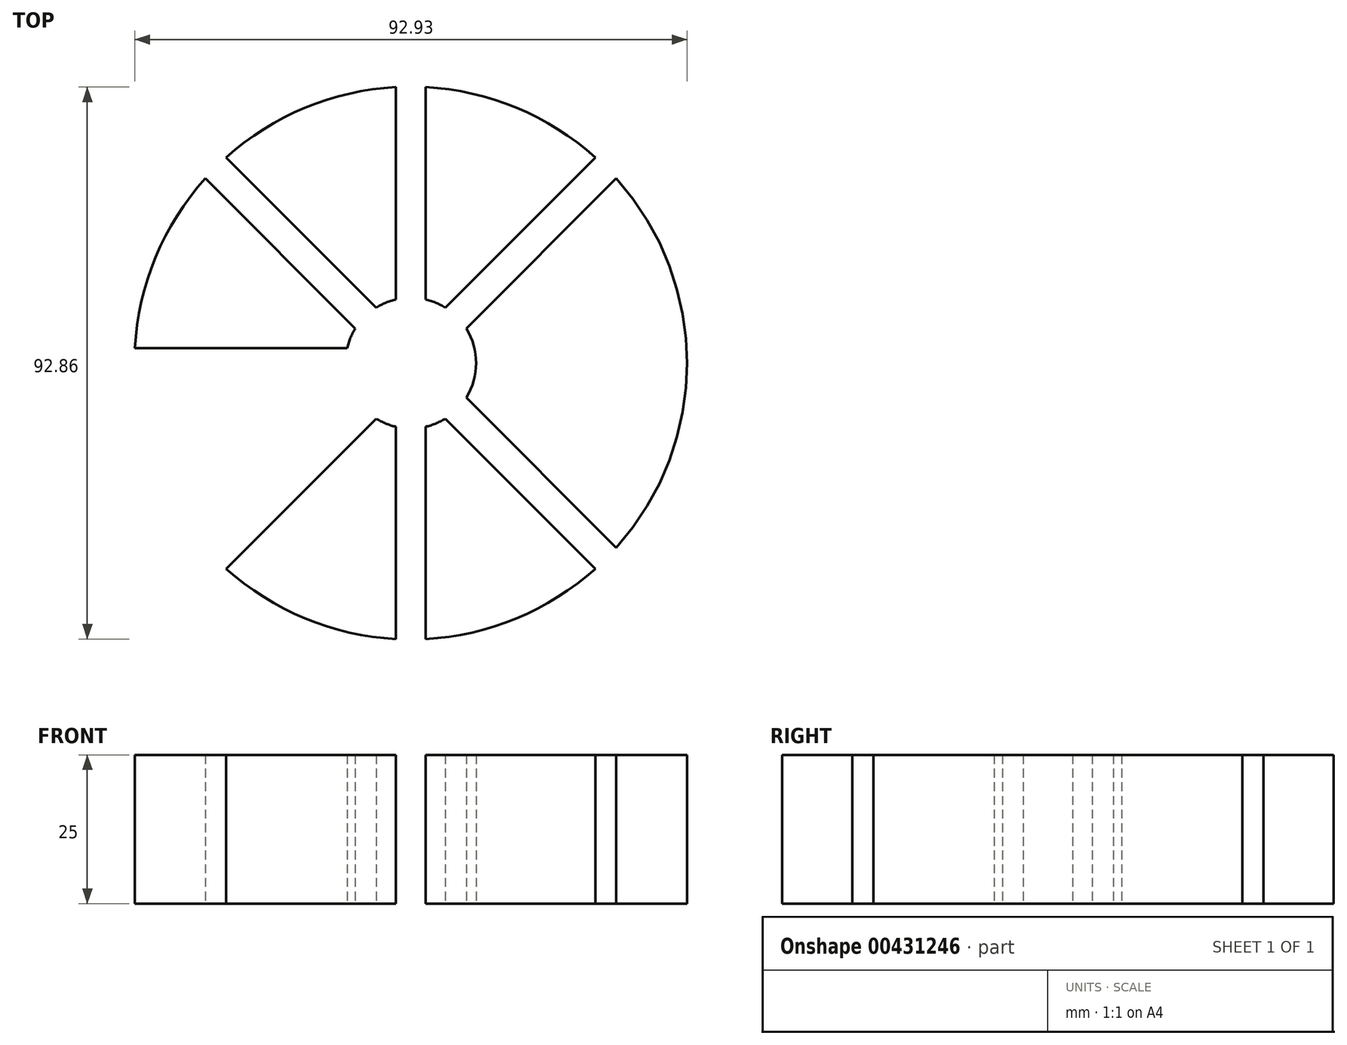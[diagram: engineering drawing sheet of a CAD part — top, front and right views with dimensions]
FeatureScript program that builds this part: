
annotation { "Feature Type Name" : "Feature", "Feature Type Description" : "" }
export const myFeature = defineFeature(function(context is Context, id is Id, definition is map)
    precondition{}
    {
        {
            var Q0;
            Q0=qCreatedBy(makeId("Top.planeOp"),FACE);
            var sketch = newSketch(context, id + "F0", { "sketchPlane" : qUnion([Q0])});
            skCircle(sketch, "E0", {"center": v(0, 0) * mm, "radius": 46.5 * mm});
            skCircle(sketch, "E1", {"center": v(0, 0) * mm, "radius": 11 * mm});
            skLineSegment(sketch, "E2.bottom", {"start": v(-2.5, 55.75) * mm, "end": v(2.5, 55.75) * mm});
            skLineSegment(sketch, "E2.top", {"start": v(-2.5, -55.75) * mm, "end": v(2.5, -55.75) * mm});
            skLineSegment(sketch, "E2.left", {"start": v(-2.5, 55.75) * mm, "end": v(-2.5, -55.75) * mm});
            skLineSegment(sketch, "E2.right", {"start": v(2.5, 55.75) * mm, "end": v(2.5, -55.75) * mm});
            skLineSegment(sketch, "E3.1.0", {"start": v(37.65, 41.19) * mm, "end": v(-41.19, -37.65) * mm});
            skLineSegment(sketch, "E3.1.1", {"start": v(41.19, 37.65) * mm, "end": v(-37.65, -41.19) * mm});
            skLineSegment(sketch, "E3.1.2", {"start": v(-41.19, -37.65) * mm, "end": v(-37.65, -41.19) * mm});
            skLineSegment(sketch, "E3.1.3", {"start": v(37.65, 41.19) * mm, "end": v(41.19, 37.65) * mm});
            skLineSegment(sketch, "E3.2.0", {"start": v(55.75, 2.5) * mm, "end": v(-55.75, 2.5) * mm});
            skLineSegment(sketch, "E3.2.1", {"start": v(55.75, -2.5) * mm, "end": v(-55.75, -2.5) * mm});
            skLineSegment(sketch, "E3.2.2", {"start": v(-55.75, 2.5) * mm, "end": v(-55.75, -2.5) * mm});
            skLineSegment(sketch, "E3.2.3", {"start": v(55.75, 2.5) * mm, "end": v(55.75, -2.5) * mm});
            skLineSegment(sketch, "E3.3.0", {"start": v(41.19, -37.65) * mm, "end": v(-37.65, 41.19) * mm});
            skLineSegment(sketch, "E3.3.1", {"start": v(37.65, -41.19) * mm, "end": v(-41.19, 37.65) * mm});
            skLineSegment(sketch, "E3.3.2", {"start": v(-37.65, 41.19) * mm, "end": v(-41.19, 37.65) * mm});
            skLineSegment(sketch, "E3.3.3", {"start": v(41.19, -37.65) * mm, "end": v(37.65, -41.19) * mm});
            skLineSegment(sketch, "E3.anchor1", {"start": v(0, 0) * mm, "end": v(-2.5, -55.75) * mm, "construction": true});
            skLineSegment(sketch, "E3.anchor2", {"start": v(0, 0) * mm, "end": v(-37.65, 41.19) * mm, "construction": true});
            skSolve(sketch);
        }
        {
            var Q0;
            {var subQ0=sQuery(id+"F0.wireOp",EDGE,"E3.3.1");var subQ1=sQuery(id+"F0.wireOp",EDGE,"E0");var subQ2=makeQuery(id+"F0.imprint","INTERSECT",VERTEX,{"disambiguationData":[OD(0.0)],"derivedFrom":[subQ1,subQ0]});Q0=makeQuery(id+"F0.imprint","IMPRINT",FACE,{"disambiguationData":[TD([[makeQuery(id+"F0.imprint","IMPRINT",EDGE,{"disambiguationData":[TD([[subQ2,-1.0]])],"derivedFrom":subQ1}),1.0]])]});}
            var Q1;
            {var subQ0=sQuery(id+"F0.wireOp",EDGE,"E2.left");var subQ1=sQuery(id+"F0.wireOp",EDGE,"E0");var subQ2=makeQuery(id+"F0.imprint","INTERSECT",VERTEX,{"disambiguationData":[OD(0.0)],"derivedFrom":[subQ1,subQ0]});Q1=makeQuery(id+"F0.imprint","IMPRINT",FACE,{"disambiguationData":[TD([[makeQuery(id+"F0.imprint","IMPRINT",EDGE,{"disambiguationData":[TD([[subQ2,-1.0]])],"derivedFrom":subQ1}),1.0]])]});}
            var Q2;
            {var subQ0=sQuery(id+"F0.wireOp",EDGE,"E3.1.0");var subQ1=sQuery(id+"F0.wireOp",EDGE,"E0");var subQ2=makeQuery(id+"F0.imprint","INTERSECT",VERTEX,{"disambiguationData":[OD(0.0)],"derivedFrom":[subQ1,subQ0]});Q2=makeQuery(id+"F0.imprint","IMPRINT",FACE,{"disambiguationData":[TD([[makeQuery(id+"F0.imprint","IMPRINT",EDGE,{"disambiguationData":[TD([[subQ2,-1.0]])],"derivedFrom":subQ1}),1.0]])]});}
            var Q3;
            {var subQ0=sQuery(id+"F0.wireOp",EDGE,"E3.1.1");var subQ1=sQuery(id+"F0.wireOp",EDGE,"E0");var subQ2=makeQuery(id+"F0.imprint","INTERSECT",VERTEX,{"disambiguationData":[OD(0.0)],"derivedFrom":[subQ1,subQ0]});Q3=makeQuery(id+"F0.imprint","IMPRINT",FACE,{"disambiguationData":[TD([[makeQuery(id+"F0.imprint","IMPRINT",EDGE,{"disambiguationData":[TD([[subQ2,1.0]])],"derivedFrom":subQ1}),1.0]])]});}
            var Q4;
            {var subQ0=sQuery(id+"F0.wireOp",EDGE,"E3.3.0");var subQ1=sQuery(id+"F0.wireOp",EDGE,"E0");var subQ2=makeQuery(id+"F0.imprint","INTERSECT",VERTEX,{"disambiguationData":[OD(1.0)],"derivedFrom":[subQ1,subQ0]});Q4=makeQuery(id+"F0.imprint","IMPRINT",FACE,{"disambiguationData":[TD([[makeQuery(id+"F0.imprint","IMPRINT",EDGE,{"disambiguationData":[TD([[subQ2,-1.0]])],"derivedFrom":subQ1}),1.0]])]});}
            var Q5;
            {var subQ0=sQuery(id+"F0.wireOp",EDGE,"E2.right");var subQ1=sQuery(id+"F0.wireOp",EDGE,"E0");var subQ2=makeQuery(id+"F0.imprint","INTERSECT",VERTEX,{"disambiguationData":[OD(1.0)],"derivedFrom":[subQ1,subQ0]});Q5=makeQuery(id+"F0.imprint","IMPRINT",FACE,{"disambiguationData":[TD([[makeQuery(id+"F0.imprint","IMPRINT",EDGE,{"disambiguationData":[TD([[subQ2,-1.0]])],"derivedFrom":subQ1}),1.0]])]});}
            var Q6;
            {var subQ0=sQuery(id+"F0.wireOp",EDGE,"E3.1.1");var subQ1=sQuery(id+"F0.wireOp",EDGE,"E0");var subQ2=makeQuery(id+"F0.imprint","INTERSECT",VERTEX,{"disambiguationData":[OD(1.0)],"derivedFrom":[subQ1,subQ0]});Q6=makeQuery(id+"F0.imprint","IMPRINT",FACE,{"disambiguationData":[TD([[makeQuery(id+"F0.imprint","IMPRINT",EDGE,{"disambiguationData":[TD([[subQ2,-1.0]])],"derivedFrom":subQ1}),1.0]])]});}
            var Q7;
            {var subQ0=sQuery(id+"F0.wireOp",EDGE,"E3.2.1");var subQ1=sQuery(id+"F0.wireOp",EDGE,"E0");var subQ2=makeQuery(id+"F0.imprint","INTERSECT",VERTEX,{"disambiguationData":[OD(0.0)],"derivedFrom":[subQ1,subQ0]});Q7=makeQuery(id+"F0.imprint","IMPRINT",FACE,{"disambiguationData":[TD([[makeQuery(id+"F0.imprint","IMPRINT",EDGE,{"disambiguationData":[TD([[subQ2,-1.0]])],"derivedFrom":subQ1}),1.0]])]});}
            extrude(context, id + "F1", {"entities" : qUnion([Q0, Q1, Q2, Q3, Q4, Q5, Q6, Q7]), "depth" : 25 * mm});
        }
    });
